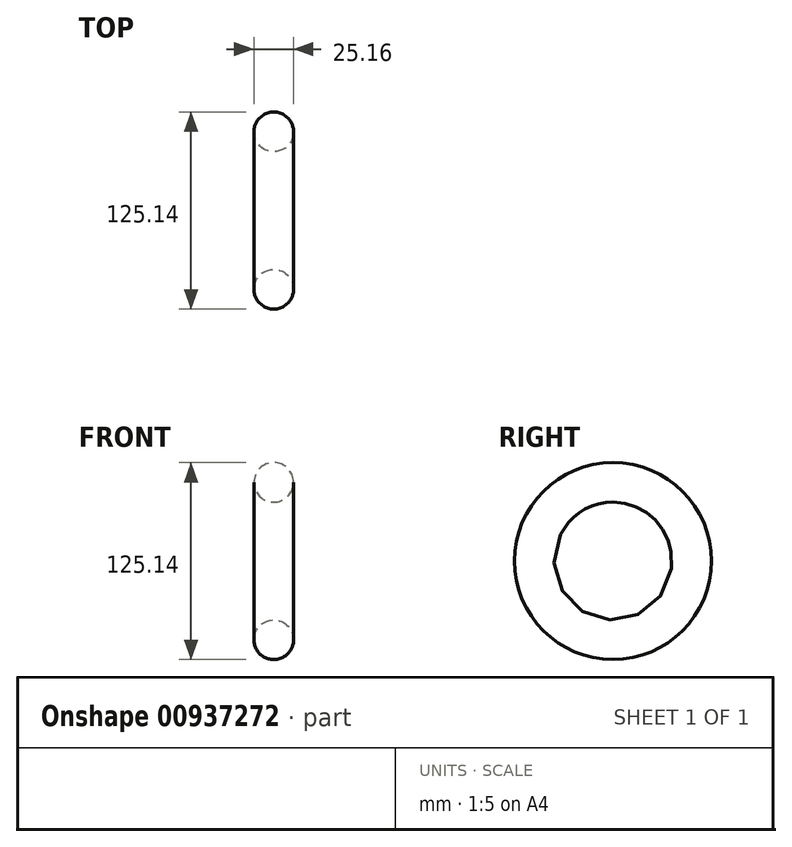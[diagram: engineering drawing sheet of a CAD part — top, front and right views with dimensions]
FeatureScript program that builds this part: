
annotation { "Feature Type Name" : "Feature", "Feature Type Description" : "" }
export const myFeature = defineFeature(function(context is Context, id is Id, definition is map)
    precondition{}
    {
        {
            var Q0;
            Q0=qCreatedBy(makeId("Front.planeOp"),FACE);
            var sketch = newSketch(context, id + "F0", { "sketchPlane" : qUnion([Q0])});
            skCircle(sketch, "E0", {"center": v(0, 49.99) * mm, "radius": 12.58 * mm});
            skLineSegment(sketch, "E1", {"start": v(-21.85, 0) * mm, "end": v(28.45, 0) * mm});
            skSolve(sketch);
        }
        {
            var Q0;
            Q0 = qSketchRegion(id + "F0", true);
            var Q1;
            Q1=sQuery(id+"F0.wireOp",EDGE,"E1");
            revolve(context, id + "F1", {"surfaceOperationType" : NewSurfaceOperationType.NEW, "entities" : qUnion([Q0]), "axis" : qUnion([Q1]), "revolveType" : RevolveType.FULL});
        }
    });
